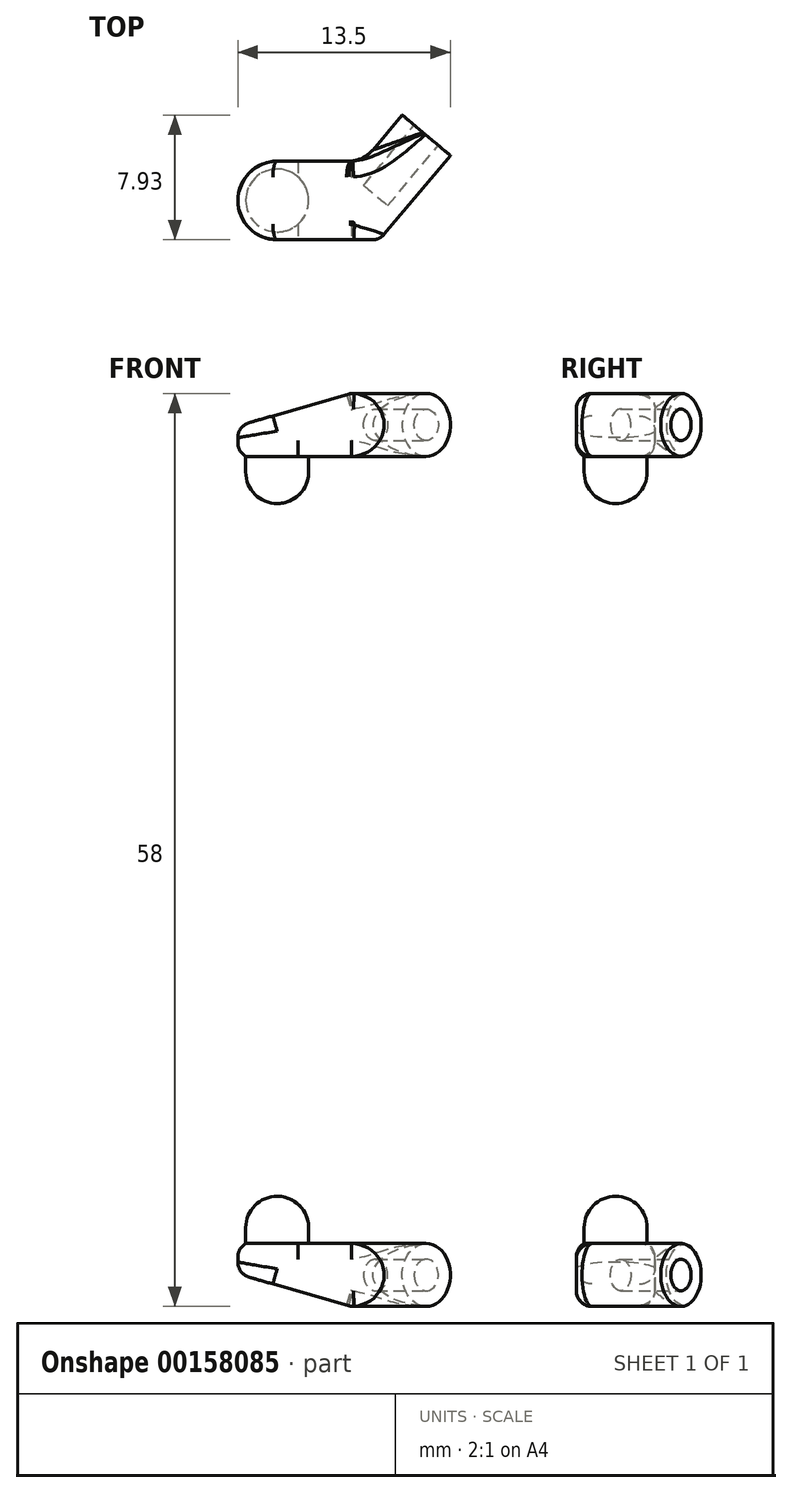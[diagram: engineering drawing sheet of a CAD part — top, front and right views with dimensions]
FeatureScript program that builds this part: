
annotation { "Feature Type Name" : "Feature", "Feature Type Description" : "" }
export const myFeature = defineFeature(function(context is Context, id is Id, definition is map)
    precondition{}
    {
        {
            var Q0;
            Q0=qCreatedBy(makeId("Top.planeOp"),FACE);
            var sketch = newSketch(context, id + "F0", { "sketchPlane" : qUnion([Q0])});
            skCircle(sketch, "E0", {"center": v(0, 0) * mm, "radius": 2 * mm});
            skSolve(sketch);
        }
        {
            var Q0;
            Q0=makeQuery(id+"F0.imprint","IMPRINT",FACE,{"disambiguationData":[TD([[makeQuery(id+"F0.imprint","IMPRINT",EDGE,{"derivedFrom":sQuery(id+"F0.wireOp",EDGE,"E0")}),1.0]])]});
            extrude(context, id + "F1", {"entities" : qUnion([Q0]), "depth" : 3 * mm});
        }
        {
            var Q0;
            Q0=makeQuery(id+"F1.opExtrude","CAP_FACE",FACE,{"disambiguationData":[OSD([sQuery(id+"F0.wireOp",EDGE,"E0")])],"isStart":false});
            var sketch = newSketch(context, id + "F2", { "sketchPlane" : qUnion([Q0])});
            skArc(sketch, "E1", {"start": v(0, 2.5) * mm, "mid": v(-2.5, 0) * mm, "end": v(0, -2.5) * mm});
            skLineSegment(sketch, "E2", {"start": v(0, -2.5) * mm, "end": v(6.5, -2.5) * mm});
            skLineSegment(sketch, "E3", {"start": v(0, 2.5) * mm, "end": v(5.47, 2.5) * mm});
            skLineSegment(sketch, "E4", {"start": v(6.5, -2.5) * mm, "end": v(11, 2.86) * mm});
            skLineSegment(sketch, "E5", {"start": v(11, 2.86) * mm, "end": v(7.94, 5.43) * mm});
            skLineSegment(sketch, "E6", {"start": v(7.94, 5.43) * mm, "end": v(5.47, 2.5) * mm});
            skSolve(sketch);
        }
        {
            var Q0;
            Q0=makeQuery(id+"F2.imprint","IMPRINT",FACE,{"disambiguationData":[TD([[makeQuery(id+"F2.imprint","IMPRINT",EDGE,{"derivedFrom":sQuery(id+"F2.wireOp",EDGE,"E1")}),1.0]])]});
            var Q1;
            Q1=makeQuery(id+"F2.imprint","IMPRINT",FACE,{"disambiguationData":[TD([[makeQuery(id+"F2.imprint","IMPRINT",EDGE,{"derivedFrom":makeQuery(id+"F1.opExtrude","CAP_EDGE",EDGE,{"disambiguationData":[OSD([sQuery(id+"F0.wireOp",EDGE,"E0")])],"isStart":false})}),1.0]])]});
            extrude(context, id + "F3", {"entities" : qUnion([Q0, Q1]), "operationType" : NewBodyOperationType.ADD, "depth" : 4 * mm});
        }
        {
            var Q0;
            Q0=makeQuery(id+"F3.opExtrude","CAP_EDGE",EDGE,{"disambiguationData":[OSD([sQuery(id+"F2.wireOp",EDGE,"E4")])],"isStart":false});
            var Q1;
            Q1=makeQuery(id+"F3.opExtrude","CAP_EDGE",EDGE,{"disambiguationData":[OSD([sQuery(id+"F2.wireOp",EDGE,"E4")])],"isStart":true});
            var Q2;
            Q2=makeQuery(id+"F3.opExtrude","CAP_EDGE",EDGE,{"disambiguationData":[OSD([sQuery(id+"F2.wireOp",EDGE,"E6")])],"isStart":false});
            var Q3;
            Q3=makeQuery(id+"F3.opExtrude","CAP_EDGE",EDGE,{"disambiguationData":[OSD([sQuery(id+"F2.wireOp",EDGE,"E6")])],"isStart":true});
            fillet(context, id + "F4", {"entities" : qUnion([Q0, Q1, Q2, Q3]), "radius" : 2 * mm, "tangentPropagation" : true, "allowEdgeOverflow" : false});
        }
        {
            var Q0;
            Q0=makeQuery(id+"F4.opFillet","BLEND_EDGE",EDGE,{"blendedFrom":[makeQuery(id+"F3.opExtrude","CAP_EDGE",EDGE,{"disambiguationData":[OSD([sQuery(id+"F2.wireOp",EDGE,"E6")])],"isStart":true}),makeQuery(id+"F3.opExtrude","SWEPT_FACE",FACE,{"disambiguationData":[OSD([sQuery(id+"F2.wireOp",EDGE,"E3")])]})],"blendedInto":[makeQuery(id+"F3.opExtrude","SWEPT_FACE",FACE,{"disambiguationData":[OSD([sQuery(id+"F2.wireOp",EDGE,"E3")])]})]});
            fillet(context, id + "F5", {"entities" : qUnion([Q0]), "radius" : 2 * mm, "tangentPropagation" : true, "allowEdgeOverflow" : false});
        }
        {
            var Q0;
            Q0=makeQuery(id+"F3.opExtrude","CAP_EDGE",EDGE,{"disambiguationData":[OSD([sQuery(id+"F2.wireOp",EDGE,"E3")])],"isStart":false});
            fillet(context, id + "F6", {"entities" : qUnion([Q0]), "radius" : 1 * mm, "tangentPropagation" : true, "allowEdgeOverflow" : false});
        }
        {
            var Q0;
            Q0=makeQuery(id+"F1.opExtrude","CAP_EDGE",EDGE,{"disambiguationData":[OSD([sQuery(id+"F0.wireOp",EDGE,"E0")])],"isStart":true});
            fillet(context, id + "F7", {"entities" : qUnion([Q0]), "radius" : 2 * mm, "tangentPropagation" : true, "allowEdgeOverflow" : false});
        }
        {
            var Q0;
            Q0=makeQuery(id+"F3.opExtrude","SWEPT_FACE",FACE,{"disambiguationData":[OSD([sQuery(id+"F2.wireOp",EDGE,"E5")])]});
            var sketch = newSketch(context, id + "F8", { "sketchPlane" : qUnion([Q0])});
            skCircle(sketch, "E7", {"center": v(-4.59, 5) * mm, "radius": 1 * mm});
            skSolve(sketch);
        }
        {
            var Q0;
            Q0=makeQuery(id+"F8.imprint","IMPRINT",FACE,{"disambiguationData":[TD([[makeQuery(id+"F8.imprint","IMPRINT",EDGE,{"derivedFrom":sQuery(id+"F8.wireOp",EDGE,"E7")}),1.0]])]});
            extrude(context, id + "F9", {"entities" : qUnion([Q0]), "operationType" : NewBodyOperationType.REMOVE, "oppositeDirection" : true, "depth" : 5 * mm});
        }
        {
            var Q0;
            Q0=makeQuery(id+"F3.opExtrude","SWEPT_FACE",FACE,{"disambiguationData":[OSD([sQuery(id+"F2.wireOp",EDGE,"E3")])]});
            var sketch = newSketch(context, id + "F10", { "sketchPlane" : qUnion([Q0])});
            skPoint(sketch, "E8.0", {"position": v(-4.7, 7) * mm});
            skLineSegment(sketch, "E9", {"start": v(2.5, 6) * mm, "end": v(2.5, 3.87) * mm});
            skLineSegment(sketch, "E10", {"start": v(-4.7, 7) * mm, "end": v(2.5, 4.93) * mm});
            skLineSegment(sketch, "E11", {"start": v(2.5, 4.93) * mm, "end": v(3.1, 7) * mm});
            skLineSegment(sketch, "E12", {"start": v(3.1, 7) * mm, "end": v(-4.7, 7) * mm});
            skSolve(sketch);
        }
        {
            var Q0;
            {var subQ0=sQuery(id+"F10.wireOp",EDGE,"E10");var subQ1=sQuery(id+"F2.wireOp",EDGE,"E3");var subQ2=makeQuery(id+"F6.opFillet","BLEND_EDGE",EDGE,{"blendedFrom":[makeQuery(id+"F3.opExtrude","CAP_EDGE",EDGE,{"disambiguationData":[OSD([subQ1])],"isStart":false}),makeQuery(id+"F3.opExtrude","SWEPT_FACE",FACE,{"disambiguationData":[OSD([subQ1])]})],"blendedInto":[makeQuery(id+"F3.opExtrude","SWEPT_FACE",FACE,{"disambiguationData":[OSD([subQ1])]})]});var subQ3=makeQuery(id+"F10.imprint","INTERSECT",VERTEX,{"derivedFrom":[subQ2,subQ0]});Q0=makeQuery(id+"F10.imprint","IMPRINT",FACE,{"disambiguationData":[TD([[makeQuery(id+"F10.imprint","IMPRINT",EDGE,{"disambiguationData":[TD([[subQ3,-1.0]])],"derivedFrom":subQ0}),1.0]])]});}
            var Q1;
            {var subQ1=sQuery(id+"F10.wireOp",EDGE,"E11");Q1=makeQuery(id+"F10.imprint","IMPRINT",FACE,{"disambiguationData":[TD([[makeQuery(id+"F10.imprint","IMPRINT",EDGE,{"derivedFrom":subQ1}),1.0]])]});}
            extrude(context, id + "F11", {"entities" : qUnion([Q0, Q1]), "operationType" : NewBodyOperationType.REMOVE, "oppositeDirection" : true, "depth" : 25 * mm});
        }
        {
            var Q0;
            {var subQ0=sQuery(id+"F2.wireOp",EDGE,"E2");Q0=makeQuery(id+"F11.boolean.opBoolean","INTERSECT",EDGE,{"derivedFrom":[makeQuery(id+"F6.opFillet","BLEND_FACE",FACE,{"disambiguationData":[OSD([subQ0]),TDD([makeQuery(id+"F3.opExtrude","CAP_EDGE",EDGE,{"disambiguationData":[OSD([subQ0])],"isStart":false})])]}),makeQuery(id+"F11.opExtrude","SWEPT_FACE",FACE,{"disambiguationData":[OSD([sQuery(id+"F10.wireOp",EDGE,"E10")])]})]});}
            fillet(context, id + "F12", {"entities" : qUnion([Q0]), "radius" : 1 * mm, "tangentPropagation" : true, "allowEdgeOverflow" : false});
        }
        {
            var Q0;
            Q0=makeQuery(id+"F3.opExtrude","CAP_FACE",FACE,{"disambiguationData":[OSD([sQuery(id+"F2.wireOp",EDGE,"E1"),sQuery(id+"F2.wireOp",EDGE,"E2"),sQuery(id+"F2.wireOp",EDGE,"E3"),sQuery(id+"F2.wireOp",EDGE,"E4"),sQuery(id+"F2.wireOp",EDGE,"E5"),sQuery(id+"F2.wireOp",EDGE,"E6")])],"isStart":true});
            cPlane(context, id + "F13", {"entities" : qUnion([Q0]), "cplaneType" : CPlaneType.OFFSET, "offset" : 25 * mm, "width" : 150 * mm, "height" : 150 * mm});
        }
        {
            var Q0;
            Q0=makeQuery(id+"F1.opExtrude","SWEPT_BODY",BODY,{"disambiguationData":[OSD([sQuery(id+"F0.wireOp",EDGE,"E0")])]});
            var Q1;
            Q1=qCreatedBy(id+"F13.planeOp",FACE);
            mirror(context, id + "F14", {"entities" : qUnion([Q0]), "mirrorPlane" : qUnion([Q1])});
        }
    });
